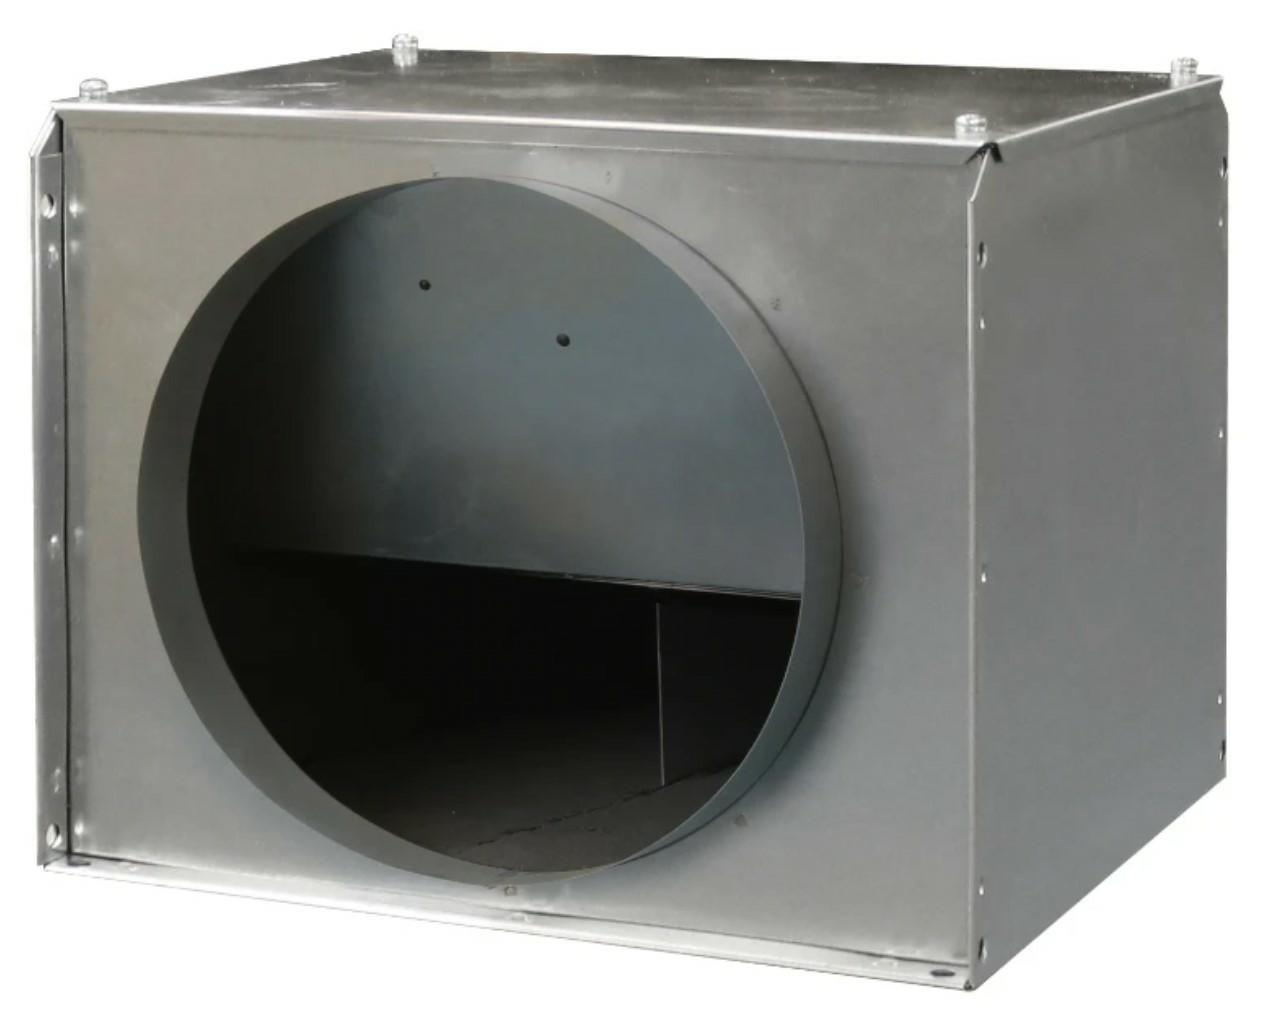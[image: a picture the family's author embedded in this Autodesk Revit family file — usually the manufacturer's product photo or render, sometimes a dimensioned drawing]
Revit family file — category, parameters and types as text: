
# Revit family: CADS_Vent-Axia_MechEquip_Fan_QP_QuietPackAcoustic - SUPPLY
name_source: partatom
category: Mechanical Equipment
units: mm (PartAtom-declared; Revit-internal decimal feet)

## family parameters
Classification = None
Cut with Voids When Loaded = No
Host = Face
OmniClass Number = 23.75.35.17.11
OmniClass Title = Fans for Air Ductwork
Part Type = Normal
Room Calculation Point = No
Round Connector Dimension = Use Diameter
Shared = No

## types (9) — shared parameters
AirflowRateRange = 0.0 L/s
AssemblyPlace = UNKNOWN
AssetType = FIXED
Default Elevation = 1219 mm
DurationUnit = Year
EBHoffset = 110 mm
EBVoffset = 55 mm
ExteriorInsulation = No
Fitting Type = Ignore
GrossWeight = 0.00 kg
HasProtectiveEarth = No
IsExtendedWarranty = No
ManufacturerAddress = Fleming Way
Crawley 
RH10 9YX
Quantity = 1
RatedCurrent = 0 A
RatedVoltage = 0 V
Status = New
WarrantyGuarantor = Vent-Axia Limited
WorkingPressure = 0.0 Pa
zero-valued in all types: CADS_Index, CADS_Usage, ExpectedServiceLife, H, NumberOfPoles, W

## per-type parameters (varying)
| type | L | ModelReference | NominalDiameter | NominalHeight | NominalLength | NominalWidth | OutOffset | OverallLength | SpigotCLHeight | SpigotLength | Type Image |
| QP100C | 360 mm | ACOUSTIC BOX FAN, 100 DIA SPIGOTS | 100 mm  [stored 0.328084 ft] | 190 mm | 400 mm | 310 mm | 111 mm | 460 mm | 94 mm | 30 mm  [stored 0.0984252 ft] | <None> |
| QP125C | 360 mm | ACOUSTIC BOX FAN, 125 DIA SPIGOTS | 125 mm  [stored 0.410105 ft] | 190 mm | 400 mm | 310 mm | 111 mm | 460 mm | 94 mm | 30 mm  [stored 0.0984252 ft] | <None> |
| QP150C | 360 mm | ACOUSTIC BOX FAN, 150 DIA SPIGOTS | 150 mm | 190 mm | 400 mm | 310 mm | 111 mm | 460 mm | 94 mm | 30 mm  [stored 0.0984252 ft] | <None> |
| QP160C | 360 mm | ACOUSTIC BOX FAN, 160 DIA SPIGOTS | 160 mm | 190 mm | 400 mm | 310 mm | 111 mm | 460 mm | 94 mm | 30 mm  [stored 0.0984252 ft] | <None> |
| QP200C | 415 mm | ACOUSTIC BOX FAN, 200 DIA SPIGOTS | 200 mm  [stored 0.656168 ft] | 285 mm | 455 mm | 364 mm | 127 mm | 515 mm | 141 mm | 30 mm  [stored 0.0984252 ft] | <None> |
| QP250C | 415 mm | ACOUSTIC BOX FAN, 250 DIA SPIGOTS | 250 mm  [stored 0.82021 ft] | 285 mm | 455 mm | 364 mm | 127 mm | 515 mm | 141 mm | 30 mm  [stored 0.0984252 ft] | <None> |
| QP315C | 690 mm | ACOUSTIC BOX FAN,315 DIA SPIGOTS | 315 mm | 456 mm | 730 mm | 572 mm | 243 mm | 792 mm | 227 mm | 31 mm | <None> |
| QP400C | 690 mm | ACOUSTIC BOX FAN, 400 DIA SPIGOTS | 400 mm | 456 mm | 730 mm | 572 mm | 243 mm | 792 mm | 227 mm | 31 mm | <None> |
| QP500C | 878 mm  [stored 2.88058 ft] | ACOUSTIC BOX FAN, 500 DIA SPIGOTS | 500 mm  [stored 1.64042 ft] | 575 mm  [stored 1.88648 ft] | 918 mm | 769 mm  [stored 2.52297 ft] | 326 mm  [stored 1.06955 ft] | 1006 mm | 286 mm | 44 mm | CADS_Vent-Axia_MechEquip_Fan_QP_QuietPackAcoustic.jpg |

note: column(s) folded — value = type name in every type: ModelNumber

note: [stored X ft] marks values corroborated as IEEE doubles in the binary element streams (Revit-internal decimal feet)

## geometry (parser evidence)
native form markers: Sweep x3
no freeform markers — native parametric forms only
